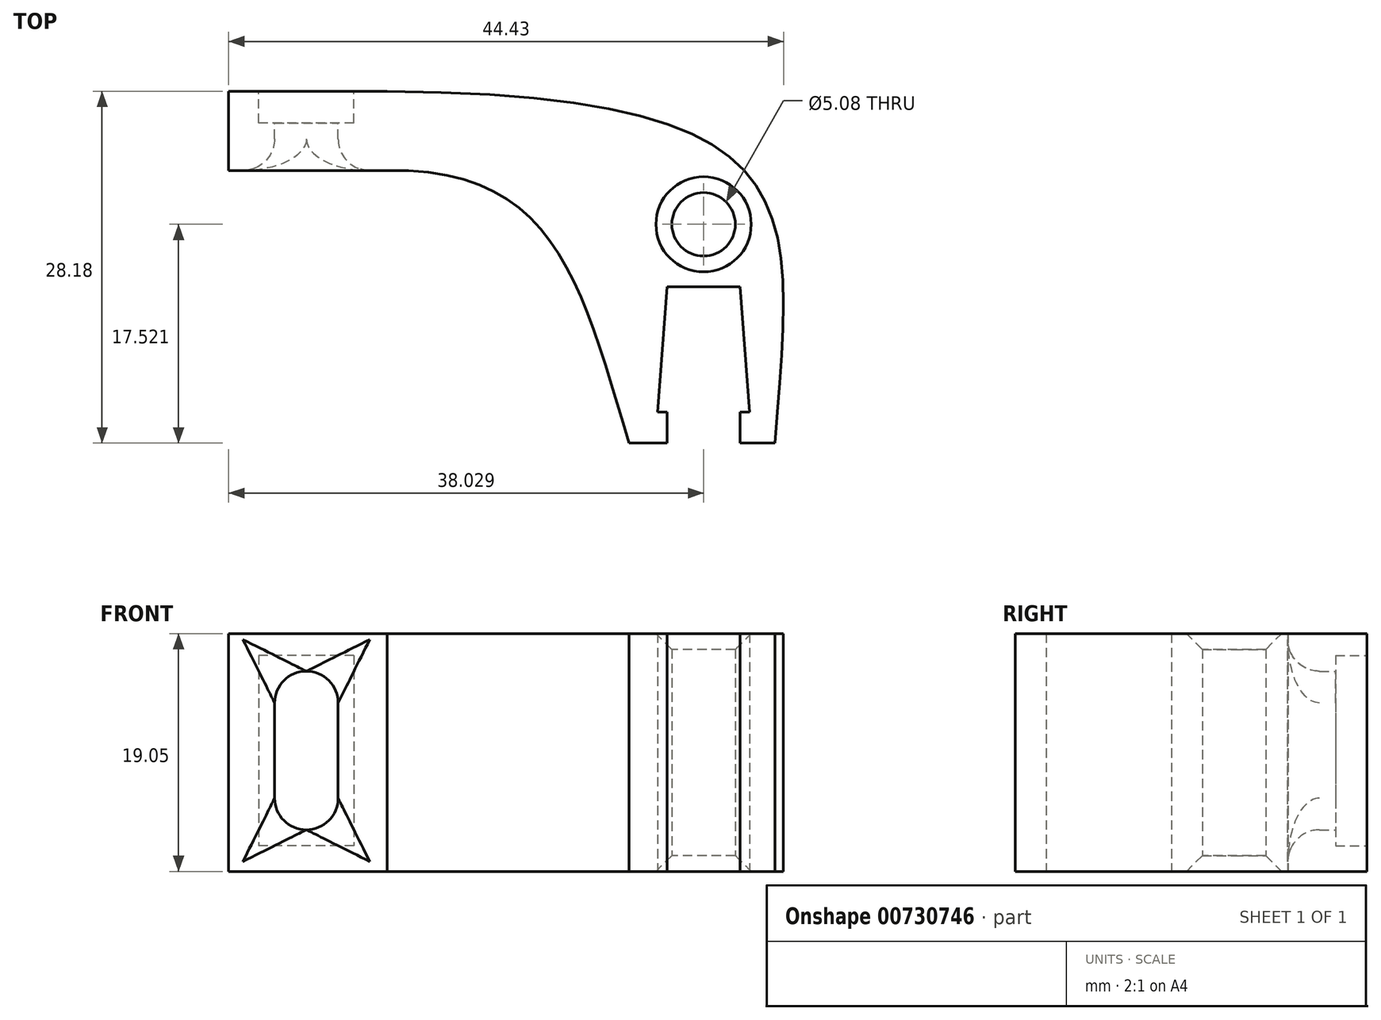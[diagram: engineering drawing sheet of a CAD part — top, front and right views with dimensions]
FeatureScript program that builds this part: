
annotation { "Feature Type Name" : "Feature", "Feature Type Description" : "" }
export const myFeature = defineFeature(function(context is Context, id is Id, definition is map)
    precondition{}
    {
        {
            var Q0;
            Q0=qCreatedBy(makeId("Top.planeOp"),FACE);
            var sketch = newSketch(context, id + "F0", { "sketchPlane" : qUnion([Q0])});
            skLineSegment(sketch, "E0.left", {"start": v(12.7, -10.01) * mm, "end": v(12.7, -12.49) * mm});
            skLineSegment(sketch, "E0.right", {"start": v(6.86, -10.01) * mm, "end": v(6.86, -12.49) * mm});
            skPoint(sketch, "E0.middle", {"position": v(9.78, -6.23) * mm});
            skLineSegment(sketch, "E1.top", {"start": v(6.86, -12.49) * mm, "end": v(3.81, -12.49) * mm});
            skLineSegment(sketch, "E2.top", {"start": v(12.7, -12.49) * mm, "end": v(15.5, -12.49) * mm});
            skLineSegment(sketch, "E3.bottom", {"start": v(-15.55, 9.34) * mm, "end": v(-28.25, 9.34) * mm});
            skLineSegment(sketch, "E3.top", {"start": v(-15.55, 15.7) * mm, "end": v(-28.25, 15.7) * mm});
            skLineSegment(sketch, "E3.right", {"start": v(-28.25, 9.34) * mm, "end": v(-28.25, 15.7) * mm});
            skPoint(sketch, "E3.middle", {"position": v(-21.9, 12.52) * mm});
            skFitSpline(sketch, "E4", {"points": [v(-15.55, 9.34) * mm, v(3.81, -12.49) * mm], "startDerivative": vector(41, 0.82) * mm, "endDerivative": vector(11.43, -37.46) * mm});
            skFitSpline(sketch, "E5", {"points": [v(-15.55, 15.7) * mm, v(15.5, -12.49) * mm], "startDerivative": vector(103.78, -1.12) * mm, "endDerivative": vector(-4.55, -58.51) * mm});
            skLineSegment(sketch, "E6.bottom", {"start": v(6.86, 0.02) * mm, "end": v(12.7, 0.02) * mm});
            skLineSegment(sketch, "E7", {"start": v(6.86, -10.01) * mm, "end": v(6.1, -10.01) * mm});
            skLineSegment(sketch, "E8", {"start": v(12.7, -10.01) * mm, "end": v(13.46, -10.01) * mm});
            skLineSegment(sketch, "E9", {"start": v(13.46, -10.01) * mm, "end": v(12.7, 0.02) * mm});
            skLineSegment(sketch, "E10", {"start": v(6.1, -10.01) * mm, "end": v(6.86, 0.02) * mm});
            skCircle(sketch, "E11", {"center": v(9.78, 5.03) * mm, "radius": 2.54 * mm});
            skSolve(sketch);
        }
        {
            var Q0;
            Q0=makeQuery(id+"F0.imprint","IMPRINT",FACE,{"disambiguationData":[TD([[makeQuery(id+"F0.imprint","IMPRINT",EDGE,{"derivedFrom":sQuery(id+"F0.wireOp",EDGE,"E1.top")}),-1.0]])]});
            extrude(context, id + "F1", {"entities" : qUnion([Q0]), "depth" : 19.05 * mm, "offsetDistance" : 25.4 * mm});
        }
        {
            var Q0;
            Q0=makeQuery(id+"F1.opExtrude","SWEPT_FACE",FACE,{"disambiguationData":[OSD([sQuery(id+"F0.wireOp",EDGE,"E3.top")])]});
            var sketch = newSketch(context, id + "F2", { "sketchPlane" : qUnion([Q0])});
            skLineSegment(sketch, "E12.bottom", {"start": v(18.22, 17.3) * mm, "end": v(25.84, 17.3) * mm});
            skLineSegment(sketch, "E12.top", {"start": v(18.22, 2.06) * mm, "end": v(25.84, 2.06) * mm});
            skLineSegment(sketch, "E12.left", {"start": v(18.22, 17.3) * mm, "end": v(18.22, 2.06) * mm});
            skLineSegment(sketch, "E12.right", {"start": v(25.84, 17.3) * mm, "end": v(25.84, 2.06) * mm});
            skPoint(sketch, "E12.middle", {"position": v(22.03, 9.68) * mm});
            skSolve(sketch);
        }
        {
            var Q0;
            Q0 = qSketchRegion(id + "F2", true);
            extrude(context, id + "F3", {"entities" : qUnion([Q0]), "operationType" : NewBodyOperationType.REMOVE, "oppositeDirection" : true, "depth" : 2.54 * mm, "offsetDistance" : 25.4 * mm});
        }
        {
            var Q0;
            Q0=makeQuery(id+"F3.boolean.opBoolean","COPY",FACE,{"derivedFrom":makeQuery(id+"F3.opExtrude","CAP_FACE",FACE,{"disambiguationData":[OSD([sQuery(id+"F2.wireOp",EDGE,"E12.bottom"),sQuery(id+"F2.wireOp",EDGE,"E12.top"),sQuery(id+"F2.wireOp",EDGE,"E12.left"),sQuery(id+"F2.wireOp",EDGE,"E12.right")])],"isStart":false})});
            var sketch = newSketch(context, id + "F4", { "sketchPlane" : qUnion([Q0])});
            skLineSegment(sketch, "E13.bottom", {"start": v(19.49, 16.03) * mm, "end": v(24.57, 16.03) * mm});
            skLineSegment(sketch, "E13.top", {"start": v(19.49, 3.33) * mm, "end": v(24.57, 3.33) * mm});
            skLineSegment(sketch, "E13.left", {"start": v(19.49, 16.03) * mm, "end": v(19.49, 3.33) * mm});
            skLineSegment(sketch, "E13.right", {"start": v(24.57, 16.03) * mm, "end": v(24.57, 3.33) * mm});
            skPoint(sketch, "E13.middle", {"position": v(22.03, 9.68) * mm});
            skPoint(sketch, "E14.start.orphan", {"position": v(22.03, 2.06) * mm});
            skSolve(sketch);
        }
        {
            var Q0;
            Q0 = qSketchRegion(id + "F4", true);
            extrude(context, id + "F5", {"entities" : qUnion([Q0]), "operationType" : NewBodyOperationType.REMOVE, "oppositeDirection" : true, "depth" : 25.4 * mm, "offsetDistance" : 25.4 * mm});
        }
        {
            var Q0;
            Q0=makeQuery(id+"F5.boolean.opBoolean","INTERSECT",EDGE,{"derivedFrom":[makeQuery(id+"F1.opExtrude","SWEPT_FACE",FACE,{"disambiguationData":[OSD([sQuery(id+"F0.wireOp",EDGE,"E3.bottom")])]}),makeQuery(id+"F5.opExtrude","SWEPT_FACE",FACE,{"disambiguationData":[OSD([sQuery(id+"F4.wireOp",EDGE,"E13.right")])]})]});
            var Q1;
            Q1=makeQuery(id+"F5.boolean.opBoolean","INTERSECT",EDGE,{"derivedFrom":[makeQuery(id+"F1.opExtrude","SWEPT_FACE",FACE,{"disambiguationData":[OSD([sQuery(id+"F0.wireOp",EDGE,"E3.bottom")])]}),makeQuery(id+"F5.opExtrude","SWEPT_FACE",FACE,{"disambiguationData":[OSD([sQuery(id+"F4.wireOp",EDGE,"E13.bottom")])]})]});
            var Q2;
            Q2=makeQuery(id+"F5.boolean.opBoolean","INTERSECT",EDGE,{"derivedFrom":[makeQuery(id+"F1.opExtrude","SWEPT_FACE",FACE,{"disambiguationData":[OSD([sQuery(id+"F0.wireOp",EDGE,"E3.bottom")])]}),makeQuery(id+"F5.opExtrude","SWEPT_FACE",FACE,{"disambiguationData":[OSD([sQuery(id+"F4.wireOp",EDGE,"E13.left")])]})]});
            var Q3;
            Q3=makeQuery(id+"F5.boolean.opBoolean","INTERSECT",EDGE,{"derivedFrom":[makeQuery(id+"F1.opExtrude","SWEPT_FACE",FACE,{"disambiguationData":[OSD([sQuery(id+"F0.wireOp",EDGE,"E3.bottom")])]}),makeQuery(id+"F5.opExtrude","SWEPT_FACE",FACE,{"disambiguationData":[OSD([sQuery(id+"F4.wireOp",EDGE,"E13.top")])]})]});
            fillet(context, id + "F6", {"entities" : qUnion([Q0, Q1, Q2, Q3]), "radius" : 2.54 * mm, "tangentPropagation" : true, "allowEdgeOverflow" : false});
        }
        {
            var Q0;
            Q0=makeQuery(id+"F5.boolean.opBoolean","COPY",EDGE,{"derivedFrom":makeQuery(id+"F5.opExtrude","SWEPT_EDGE",EDGE,{"disambiguationData":[OSD([sQuery(id+"F4.wireOp",EDGE,"E13.top"),sQuery(id+"F4.wireOp",EDGE,"E13.right")])]})});
            var Q1;
            Q1=makeQuery(id+"F5.boolean.opBoolean","COPY",EDGE,{"derivedFrom":makeQuery(id+"F5.opExtrude","SWEPT_EDGE",EDGE,{"disambiguationData":[OSD([sQuery(id+"F4.wireOp",EDGE,"E13.top"),sQuery(id+"F4.wireOp",EDGE,"E13.left")])]})});
            var Q2;
            Q2=makeQuery(id+"F5.boolean.opBoolean","COPY",EDGE,{"derivedFrom":makeQuery(id+"F5.opExtrude","SWEPT_EDGE",EDGE,{"disambiguationData":[OSD([sQuery(id+"F4.wireOp",EDGE,"E13.bottom"),sQuery(id+"F4.wireOp",EDGE,"E13.left")])]})});
            var Q3;
            Q3=makeQuery(id+"F5.boolean.opBoolean","COPY",EDGE,{"derivedFrom":makeQuery(id+"F5.opExtrude","SWEPT_EDGE",EDGE,{"disambiguationData":[OSD([sQuery(id+"F4.wireOp",EDGE,"E13.bottom"),sQuery(id+"F4.wireOp",EDGE,"E13.right")])]})});
            fillet(context, id + "F7", {"entities" : qUnion([Q0, Q1, Q2, Q3]), "radius" : 2.54 * mm, "tangentPropagation" : true, "allowEdgeOverflow" : false});
        }
        {
            var Q0;
            Q0=makeQuery(id+"F1.opExtrude","CAP_EDGE",EDGE,{"disambiguationData":[OSD([sQuery(id+"F0.wireOp",EDGE,"E11")])],"isStart":false});
            var Q1;
            Q1=makeQuery(id+"F1.opExtrude","CAP_EDGE",EDGE,{"disambiguationData":[OSD([sQuery(id+"F0.wireOp",EDGE,"E11")])],"isStart":true});
            chamfer(context, id + "F8", {"entities" : qUnion([Q0, Q1]), "width" : 1.27 * mm, "tangentPropagation" : true});
        }
    });
